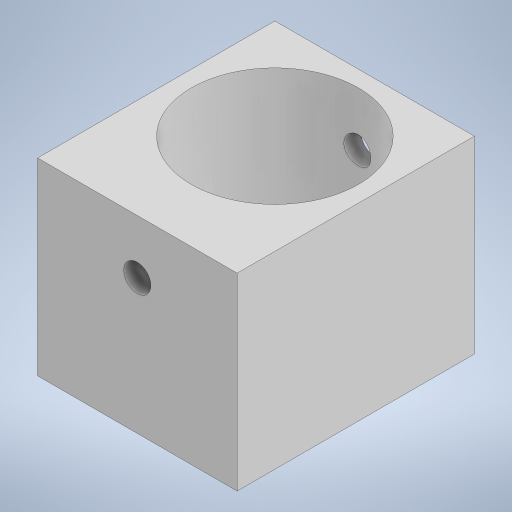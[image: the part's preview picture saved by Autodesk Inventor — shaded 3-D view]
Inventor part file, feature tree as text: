
AUTODESK INVENTOR PART (.ipt)
format: ipt  version: 2023.5 (Build 275446000, 446)  size: 236,032 bytes
history: native  units: in
note: dims shown in document units (in); Inventor stores cm internally (conversion verified against a paired STEP export)
features: extrude x7, sketch x5
ambient origin geometry x8: Origin, YZ Plane, XZ Plane, XY Plane, X Axis, Y Axis, Z Axis, Center Point
bodies: Solid1 (feature_tree)
feature tree (12):
  extrude  "Extrusion1"  Depth=1.4567in
  extrude  "Extrusion2"  Depth=0.7283in
  extrude  "Extrusion3"  Depth=1.378in TaperAngle=0.0deg
  extrude  "Extrusion4"  Depth=0.1969in TaperAngle=0.0deg
  extrude  "Extrusion5"  Depth=0.0197in TaperAngle=0.0deg
  extrude  "Extrusion6"  Depth=0.0787in TaperAngle=0.0deg
  extrude  "Extrusion7"  Depth=0.0197in TaperAngle=0.0deg
  sketch  "Sketch3"  dims[d0=1.4567in d1=1.4567in]
  sketch  "Sketch5"  dims[d2=0.7283in d3=0.7283in]
  sketch  "Sketch6"  dims[d4=1.2205in d5=1.378in d6=0.0in]
  sketch  "Sketch7"  dims[d8=0.3543in d9=0.1969in d10=0.0in]
  sketch  "Sketch8"  dims[d11=0.1969in d12=0.1969in d13=0.0in d14=0.0787in d15=0.0in d16=0.1969in d17=0.0in d18=0.7283in d19=0.7283in d22=0.3937in d24=0.1969in d25=0.3937in d26=0.7283in d27=0.0in d28=0.0in d29=0.315in d30=0.0in d21=0.0197in d23=0.0197in]
